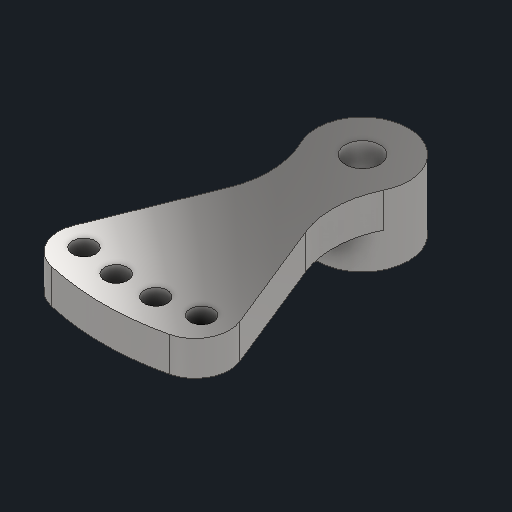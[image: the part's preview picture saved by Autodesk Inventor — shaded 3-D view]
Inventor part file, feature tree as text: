
AUTODESK INVENTOR PART (.ipt)
format: ipt  version: 2022 (Build 260153000, 153)  size: 181,760 bytes
history: native  units: mm
features: sketch x4, extrude x2, fillet x2, revolve x1, plane x1, hole x1
ambient origin geometry x8: Origin, YZ Plane, XZ Plane, XY Plane, X Axis, Y Axis, Z Axis, Center Point
bodies: Body1 (feature_tree)
feature tree (11):
  revolve  "Revolution3"  [1 undecoded]
  extrude  "Extrusion7"  Depth=45.0mm
  extrude  "Extrusion8"  TaperAngle=90.0deg  [1 undecoded]
  fillet  "Fillet3"  Radius=2.0mm
  fillet  "Fillet4"  Radius=2.0mm
  plane  "Work Plane2"
  hole  "Hole3"  [1 undecoded]
  sketch  "Sketch11"  dims[d59=3.0mm d60=6.0mm]
  sketch  "Sketch12"  dims[d61=3.0mm d62=45.0mm]
  sketch  "Sketch14"  dims[d63=2.5mm d64=90.0deg d65=2.0mm d66=2.0mm]
  sketch  "Sketch15"  dims[d67=2.0mm d68=2.0mm d71=0.872665mm d72=1.745329mm d73=1.745329mm d74=0.0mm d75=0.0mm d76=3.839724mm d77=3.839724mm d78=0.0mm d79=0.0mm d80=3.0mm d81=39.5mm d82=8.0mm d83=1.567mm d84=4.0mm d85=4.0mm d86=2.0mm d87=90.0deg d88=4.5mm d89=20.594885mm d90=10.223352mm]
note: 3 required parameter values undecoded (feature->parameter linkage not recoverable at this tier; creation-order binding heuristic only, values carry confidence <= 0.55)